# Revit family: AF-CF 36-45-56-71
name_source: partatom
category: HLS-Bauteile
revit_build: Autodesk Revit 2017 (Build: 20160720_1515(x64)
units: mm (PartAtom-declared; Revit-internal decimal feet)

## family parameters
Arbeitsebenenbasiert = Nein
Beim Laden mit Abzugskörper schneiden = Nein
Bemaßung runder Anschluss = Durchmesser verwenden
Gemeinsam genutzt = Nein
Immer vertikal = Ja
OmniClass-Nummer = 23.75.00.00
OmniClass-Titel = Climate Control (HVAC)
Raumberechnungspunkt = Nein
Teiletyp = Normal

## types (4) — shared parameters
Beschreibung = High efficiency air cooled
Condensation = Air
Depth = 660 mm
Drain pipe = 25 mm  [stored 0.082021 ft]
Gas = R410A
Gas pipe = 12.7 mm  [stored 0.0416667 ft]
Height = 203 mm  [stored 0.66601 ft]
Hersteller = Bosch
Installation = Indoor installation
Liquid pipe = 6.35 mm  [stored 0.0208333 ft]
Machine material = Galvanized Steel
Maximum Fuse Amps = 15 A
Min cable selection (power wiring) = 3×1.0 mm2
Panel color = S1004
Series = VRF
Width = 990 mm  [stored 3.24803 ft]

## per-type parameters (varying)
| type | Air Flow max | Cooling Capacity | Cooling Power Input | Heating Capacity | Heating Power Input | Minimum Circuit Amps | Net Weight | Power supply |
| AF-CF 71 | 930.00 m³/h | 7 kW | 94 W | 8 kW | 94 W | 1 A | 27.00 kg | 220-240V ~60Hz |
| AF-CF 56 | 930.00 m³/h | 6 kW | 94 W | 6 kW | 94 W | 1 A | 27.00 kg | 220-240V ~60Hz |
| AF-CF 45 | 750.00 m³/h | 5 kW | 94 W | 5 kW | 94 W | 1 A | 27.00 kg | 220-240V ~60Hz |
| AF-CF 36 | 550.00 m³/h | 4 kW | 23 W | 4 kW | 23 W | 0 A | 25.00 kg | 220-240V ~50/60Hz |

note: column(s) folded — value = type name in every type: Modell

note: [stored X ft] marks values corroborated as IEEE doubles in the binary element streams (Revit-internal decimal feet)
